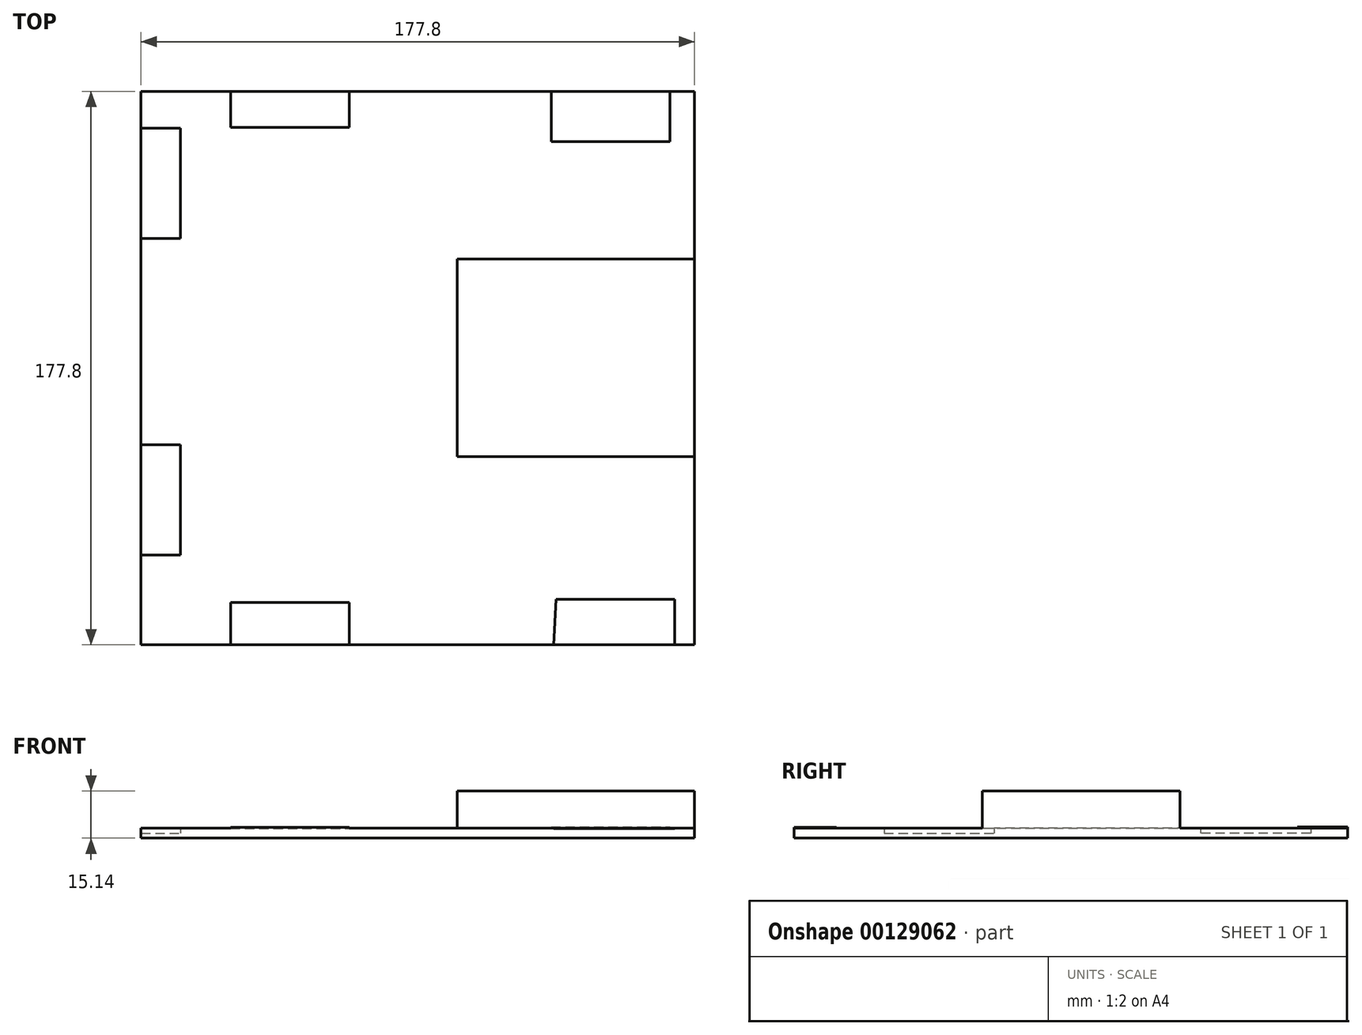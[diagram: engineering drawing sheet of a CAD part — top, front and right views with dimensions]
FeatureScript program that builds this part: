
annotation { "Feature Type Name" : "Feature", "Feature Type Description" : "" }
export const myFeature = defineFeature(function(context is Context, id is Id, definition is map)
    precondition{}
    {
        {
            var Q0;
            Q0=qCreatedBy(makeId("Top.planeOp"),FACE);
            var sketch = newSketch(context, id + "F0", { "sketchPlane" : qUnion([Q0])});
            skLineSegment(sketch, "E0.bottom", {"start": v(-96.13, 74.76) * mm, "end": v(81.67, 74.76) * mm});
            skLineSegment(sketch, "E0.top", {"start": v(-96.13, -103.04) * mm, "end": v(81.67, -103.04) * mm});
            skLineSegment(sketch, "E0.left", {"start": v(-96.13, 74.76) * mm, "end": v(-96.13, -103.04) * mm});
            skLineSegment(sketch, "E0.right", {"start": v(81.67, 74.76) * mm, "end": v(81.67, -103.04) * mm});
            skLineSegment(sketch, "E1", {"start": v(-96.13, -74.14) * mm, "end": v(-83.43, -74.14) * mm});
            skLineSegment(sketch, "E2", {"start": v(-83.43, -74.14) * mm, "end": v(-83.43, -38.8) * mm});
            skLineSegment(sketch, "E3", {"start": v(-83.43, -38.8) * mm, "end": v(-96.13, -38.8) * mm});
            skLineSegment(sketch, "E4", {"start": v(-96.13, 62.9) * mm, "end": v(-83.43, 62.9) * mm});
            skLineSegment(sketch, "E5", {"start": v(-83.43, 62.9) * mm, "end": v(-83.43, 27.55) * mm});
            skLineSegment(sketch, "E6", {"start": v(-83.43, 27.55) * mm, "end": v(-96.13, 27.55) * mm});
            skLineSegment(sketch, "E7", {"start": v(81.67, -42.55) * mm, "end": v(5.47, -42.55) * mm});
            skLineSegment(sketch, "E8", {"start": v(5.47, -42.55) * mm, "end": v(5.47, 20.95) * mm});
            skLineSegment(sketch, "E9", {"start": v(5.47, 20.95) * mm, "end": v(81.67, 20.95) * mm});
            skLineSegment(sketch, "E10", {"start": v(35.6, 74.76) * mm, "end": v(35.6, 58.63) * mm});
            skLineSegment(sketch, "E11", {"start": v(35.6, 58.63) * mm, "end": v(73.7, 58.63) * mm});
            skLineSegment(sketch, "E12", {"start": v(73.7, 58.63) * mm, "end": v(73.7, 74.76) * mm});
            skLineSegment(sketch, "E13", {"start": v(75.24, -103.04) * mm, "end": v(75.24, -88.36) * mm});
            skLineSegment(sketch, "E14", {"start": v(75.24, -88.36) * mm, "end": v(37.14, -88.36) * mm});
            skLineSegment(sketch, "E15", {"start": v(37.14, -88.36) * mm, "end": v(36.36, -103.04) * mm});
            skLineSegment(sketch, "E16", {"start": v(-67.37, 74.76) * mm, "end": v(-67.37, 63.26) * mm});
            skLineSegment(sketch, "E17", {"start": v(-67.37, 63.26) * mm, "end": v(-29.27, 63.26) * mm});
            skLineSegment(sketch, "E18", {"start": v(-29.27, 63.26) * mm, "end": v(-29.27, 74.76) * mm});
            skLineSegment(sketch, "E19", {"start": v(-67.28, -103.04) * mm, "end": v(-67.28, -89.5) * mm});
            skLineSegment(sketch, "E20", {"start": v(-67.28, -89.5) * mm, "end": v(-29.18, -89.5) * mm});
            skLineSegment(sketch, "E21", {"start": v(-29.18, -89.5) * mm, "end": v(-29.18, -103.04) * mm});
            skSolve(sketch);
        }
        {
            var Q0;
            {var subQ4=sQuery(id+"F0.wireOp",EDGE,"E0.bottom");Q0=makeQuery(id+"F0.imprint","IMPRINT",FACE,{"disambiguationData":[TD([[makeQuery(id+"F0.imprint","IMPRINT",EDGE,{"derivedFrom":subQ4}),-1.0]])]});}
            extrude(context, id + "F1", {"entities" : qUnion([Q0]), "depth" : 3.17 * mm});
        }
        {
            var Q0;
            {var subQ0=sQuery(id+"F0.wireOp",EDGE,"E4");Q0=makeQuery(id+"F0.imprint","IMPRINT",FACE,{"disambiguationData":[TD([[makeQuery(id+"F0.imprint","IMPRINT",EDGE,{"derivedFrom":subQ0}),-1.0]])]});}
            var Q1;
            {var subQ0=sQuery(id+"F0.wireOp",EDGE,"E1");Q1=makeQuery(id+"F0.imprint","IMPRINT",FACE,{"disambiguationData":[TD([[makeQuery(id+"F0.imprint","IMPRINT",EDGE,{"derivedFrom":subQ0}),1.0]])]});}
            extrude(context, id + "F2", {"entities" : qUnion([Q0, Q1]), "operationType" : NewBodyOperationType.ADD, "depth" : 1.59 * mm});
        }
        {
            var Q0;
            {var subQ0=sQuery(id+"F0.wireOp",EDGE,"E7");Q0=makeQuery(id+"F0.imprint","IMPRINT",FACE,{"disambiguationData":[TD([[makeQuery(id+"F0.imprint","IMPRINT",EDGE,{"derivedFrom":subQ0}),-1.0]])]});}
            extrude(context, id + "F3", {"entities" : qUnion([Q0]), "operationType" : NewBodyOperationType.ADD, "depth" : 1.59 * mm});
        }
        {
            var Q0;
            {var subQ0=sQuery(id+"F0.wireOp",EDGE,"E19");Q0=makeQuery(id+"F0.imprint","IMPRINT",FACE,{"disambiguationData":[TD([[makeQuery(id+"F0.imprint","IMPRINT",EDGE,{"derivedFrom":subQ0}),-1.0]])]});}
            extrude(context, id + "F4", {"entities" : qUnion([Q0]), "operationType" : NewBodyOperationType.ADD, "depth" : 3.42 * mm});
        }
        {
            var Q0;
            {var subQ0=sQuery(id+"F0.wireOp",EDGE,"E13");Q0=makeQuery(id+"F0.imprint","IMPRINT",FACE,{"disambiguationData":[TD([[makeQuery(id+"F0.imprint","IMPRINT",EDGE,{"derivedFrom":subQ0}),1.0]])]});}
            extrude(context, id + "F5", {"entities" : qUnion([Q0]), "operationType" : NewBodyOperationType.ADD, "depth" : 3.14 * mm});
        }
        {
            var Q0;
            {var subQ0=sQuery(id+"F0.wireOp",EDGE,"E16");Q0=makeQuery(id+"F0.imprint","IMPRINT",FACE,{"disambiguationData":[TD([[makeQuery(id+"F0.imprint","IMPRINT",EDGE,{"derivedFrom":subQ0}),1.0]])]});}
            extrude(context, id + "F6", {"entities" : qUnion([Q0]), "operationType" : NewBodyOperationType.ADD, "depth" : 3.12 * mm});
        }
        {
            var Q0;
            {var subQ0=sQuery(id+"F0.wireOp",EDGE,"E10");Q0=makeQuery(id+"F0.imprint","IMPRINT",FACE,{"disambiguationData":[TD([[makeQuery(id+"F0.imprint","IMPRINT",EDGE,{"derivedFrom":subQ0}),1.0]])]});}
            extrude(context, id + "F7", {"entities" : qUnion([Q0]), "operationType" : NewBodyOperationType.ADD, "depth" : 3.6 * mm});
        }
        {
            var Q0;
            Q0=makeQuery(id+"F3.opExtrude","CAP_FACE",FACE,{"disambiguationData":[OSD([sQuery(id+"F0.wireOp",EDGE,"E0.right"),sQuery(id+"F0.wireOp",EDGE,"E7"),sQuery(id+"F0.wireOp",EDGE,"E8"),sQuery(id+"F0.wireOp",EDGE,"E9")])],"isStart":false});
            extrude(context, id + "F8", {"entities" : qUnion([Q0]), "operationType" : NewBodyOperationType.ADD, "depth" : 13.55 * mm});
        }
    });
